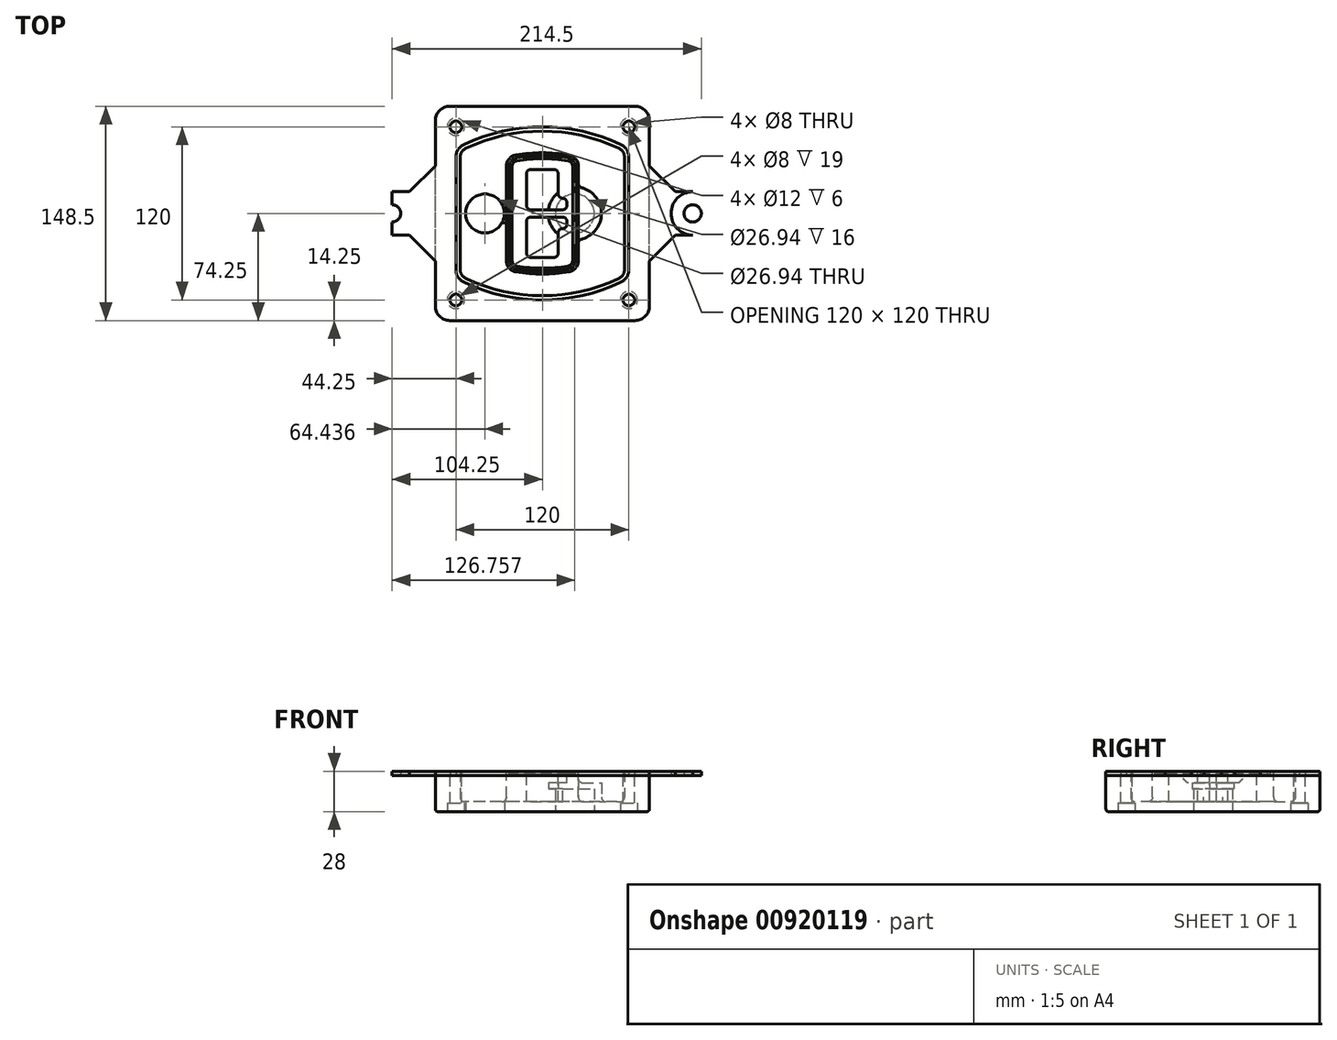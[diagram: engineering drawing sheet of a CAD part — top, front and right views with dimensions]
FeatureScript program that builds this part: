
annotation { "Feature Type Name" : "Feature", "Feature Type Description" : "" }
export const myFeature = defineFeature(function(context is Context, id is Id, definition is map)
    precondition{}
    {
        {
            var Q0;
            Q0=qCreatedBy(makeId("Top.planeOp"),FACE);
            var sketch = newSketch(context, id + "F0", { "sketchPlane" : qUnion([Q0])});
            skPoint(sketch, "E0.rect.middle", {"position": v(0, 0) * mm});
            skLineSegment(sketch, "E1.bottom", {"start": v(-64.25, -74.25) * mm, "end": v(64.25, -74.25) * mm});
            skLineSegment(sketch, "E1.top", {"start": v(-64.25, 74.25) * mm, "end": v(64.25, 74.25) * mm});
            skLineSegment(sketch, "E1.left", {"start": v(-74.25, -64.25) * mm, "end": v(-74.25, 64.25) * mm});
            skLineSegment(sketch, "E1.right", {"start": v(74.25, -64.25) * mm, "end": v(74.25, 64.25) * mm});
            skLineSegment(sketch, "E2", {"start": v(-74.25, 74.25) * mm, "end": v(74.25, -74.25) * mm, "construction": true});
            skLineSegment(sketch, "E3", {"start": v(74.25, 74.25) * mm, "end": v(-74.25, -74.25) * mm, "construction": true});
            skCircle(sketch, "E4", {"center": v(-60, 60) * mm, "radius": 4 * mm});
            skCircle(sketch, "E5", {"center": v(60, 60) * mm, "radius": 4 * mm});
            skCircle(sketch, "E6", {"center": v(60, -60) * mm, "radius": 4 * mm});
            skCircle(sketch, "E7", {"center": v(-60, -60) * mm, "radius": 4 * mm});
            skLineSegment(sketch, "E8", {"start": v(-60, 60) * mm, "end": v(60, 60) * mm, "construction": true});
            skLineSegment(sketch, "E9", {"start": v(60, 60) * mm, "end": v(60, -60) * mm, "construction": true});
            skLineSegment(sketch, "E10", {"start": v(60, -60) * mm, "end": v(-60, -60) * mm, "construction": true});
            skLineSegment(sketch, "E11", {"start": v(-60, -60) * mm, "end": v(-60, 60) * mm, "construction": true});
            skLineSegment(sketch, "E12", {"start": v(-60, 38.83) * mm, "end": v(-60, -38.83) * mm});
            skLineSegment(sketch, "E13", {"start": v(60, 38.83) * mm, "end": v(60, -38.83) * mm});
            skArc(sketch, "E14", {"start": v(54.26, 47.88) * mm, "mid": v(0, 60) * mm, "end": v(-54.26, 47.88) * mm});
            skArc(sketch, "E15", {"start": v(-54.26, -47.88) * mm, "mid": v(0, -60) * mm, "end": v(54.26, -47.88) * mm});
            skLineSegment(sketch, "E16", {"start": v(-60, 0) * mm, "end": v(60, 0) * mm, "construction": true});
            skPoint(sketch, "E17.visualSharp", {"position": v(-60, -45) * mm});
            skArc(sketch, "E17.filletArc", {"start": v(-60, -38.83) * mm, "mid": v(-58.44, -44.2) * mm, "end": v(-54.26, -47.88) * mm});
            skPoint(sketch, "E18.visualSharp", {"position": v(-60, 45) * mm});
            skArc(sketch, "E18.filletArc", {"start": v(-54.26, 47.88) * mm, "mid": v(-58.44, 44.2) * mm, "end": v(-60, 38.83) * mm});
            skPoint(sketch, "E19.visualSharp", {"position": v(60, 45) * mm});
            skArc(sketch, "E19.filletArc", {"start": v(60, 38.83) * mm, "mid": v(58.44, 44.2) * mm, "end": v(54.26, 47.88) * mm});
            skPoint(sketch, "E20.visualSharp", {"position": v(60, -45) * mm});
            skArc(sketch, "E20.filletArc", {"start": v(54.26, -47.88) * mm, "mid": v(58.44, -44.2) * mm, "end": v(60, -38.83) * mm});
            skPoint(sketch, "E21.visualSharp", {"position": v(-74.25, 74.25) * mm});
            skArc(sketch, "E21.filletArc", {"start": v(-64.25, 74.25) * mm, "mid": v(-71.32, 71.32) * mm, "end": v(-74.25, 64.25) * mm});
            skPoint(sketch, "E22.visualSharp", {"position": v(74.25, 74.25) * mm});
            skArc(sketch, "E22.filletArc", {"start": v(74.25, 64.25) * mm, "mid": v(71.32, 71.32) * mm, "end": v(64.25, 74.25) * mm});
            skPoint(sketch, "E23.visualSharp", {"position": v(74.25, -74.25) * mm});
            skArc(sketch, "E23.filletArc", {"start": v(64.25, -74.25) * mm, "mid": v(71.32, -71.32) * mm, "end": v(74.25, -64.25) * mm});
            skPoint(sketch, "E24.visualSharp", {"position": v(-74.25, -74.25) * mm});
            skArc(sketch, "E24.filletArc", {"start": v(-74.25, -64.25) * mm, "mid": v(-71.32, -71.32) * mm, "end": v(-64.25, -74.25) * mm});
            skArc(sketch, "E25.0", {"start": v(57, 38.83) * mm, "mid": v(55.9, 42.58) * mm, "end": v(52.98, 45.17) * mm});
            skLineSegment(sketch, "E25.1", {"start": v(57, 38.83) * mm, "end": v(57, -38.83) * mm});
            skArc(sketch, "E25.2", {"start": v(52.98, -45.17) * mm, "mid": v(55.9, -42.58) * mm, "end": v(57, -38.83) * mm});
            skArc(sketch, "E25.3", {"start": v(-52.98, -45.17) * mm, "mid": v(0, -57) * mm, "end": v(52.98, -45.17) * mm});
            skArc(sketch, "E25.4", {"start": v(-57, -38.83) * mm, "mid": v(-55.9, -42.58) * mm, "end": v(-52.98, -45.17) * mm});
            skArc(sketch, "E25.5", {"start": v(52.98, 45.17) * mm, "mid": v(0, 57) * mm, "end": v(-52.98, 45.17) * mm});
            skLineSegment(sketch, "E25.6", {"start": v(-57, 38.83) * mm, "end": v(-57, -38.83) * mm});
            skArc(sketch, "E25.7", {"start": v(-52.98, 45.17) * mm, "mid": v(-55.9, 42.58) * mm, "end": v(-57, 38.83) * mm});
            skArc(sketch, "E26.0", {"start": v(-55.96, 51.5) * mm, "mid": v(-61.82, 46.33) * mm, "end": v(-64, 38.83) * mm});
            skArc(sketch, "E26.1", {"start": v(55.96, 51.5) * mm, "mid": v(0, 64) * mm, "end": v(-55.96, 51.5) * mm});
            skArc(sketch, "E26.2", {"start": v(64, 38.83) * mm, "mid": v(61.82, 46.33) * mm, "end": v(55.96, 51.5) * mm});
            skLineSegment(sketch, "E26.3", {"start": v(64, 38.83) * mm, "end": v(64, -38.83) * mm});
            skArc(sketch, "E26.4", {"start": v(55.96, -51.5) * mm, "mid": v(61.82, -46.33) * mm, "end": v(64, -38.83) * mm});
            skLineSegment(sketch, "E26.5", {"start": v(-64, 38.83) * mm, "end": v(-64, -38.83) * mm});
            skArc(sketch, "E26.6", {"start": v(-55.96, -51.5) * mm, "mid": v(0, -64) * mm, "end": v(55.96, -51.5) * mm});
            skArc(sketch, "E26.7", {"start": v(-64, -38.83) * mm, "mid": v(-61.82, -46.33) * mm, "end": v(-55.96, -51.5) * mm});
            skSolve(sketch);
        }
        {
            var Q0;
            Q0=makeQuery(id+"F0.imprint","IMPRINT",FACE,{"disambiguationData":[TD([[makeQuery(id+"F0.imprint","IMPRINT",EDGE,{"derivedFrom":sQuery(id+"F0.wireOp",EDGE,"E1.bottom")}),1.0]])]});
            var Q1;
            Q1=makeQuery(id+"F0.imprint","IMPRINT",FACE,{"disambiguationData":[TD([[makeQuery(id+"F0.imprint","IMPRINT",EDGE,{"derivedFrom":sQuery(id+"F0.wireOp",EDGE,"E12")}),1.0]])]});
            var Q2;
            Q2=makeQuery(id+"F0.imprint","IMPRINT",FACE,{"disambiguationData":[TD([[makeQuery(id+"F0.imprint","IMPRINT",EDGE,{"derivedFrom":sQuery(id+"F0.wireOp",EDGE,"E25.0")}),1.0]])]});
            var Q3;
            Q3=makeQuery(id+"F0.imprint","IMPRINT",FACE,{"disambiguationData":[TD([[makeQuery(id+"F0.imprint","IMPRINT",EDGE,{"derivedFrom":sQuery(id+"F0.wireOp",EDGE,"E12")}),-1.0]])]});
            extrude(context, id + "F1", {"entities" : qUnion([Q0, Q1, Q2, Q3]), "oppositeDirection" : true, "depth" : 25 * mm});
        }
        {
            var Q0;
            Q0=makeQuery(id+"F0.imprint","IMPRINT",FACE,{"disambiguationData":[TD([[makeQuery(id+"F0.imprint","IMPRINT",EDGE,{"derivedFrom":sQuery(id+"F0.wireOp",EDGE,"E12")}),1.0]])]});
            extrude(context, id + "F2", {"entities" : qUnion([Q0]), "operationType" : NewBodyOperationType.ADD, "depth" : 3 * mm});
        }
        {
            var Q0;
            Q0=makeQuery(id+"F0.imprint","IMPRINT",FACE,{"disambiguationData":[TD([[makeQuery(id+"F0.imprint","IMPRINT",EDGE,{"derivedFrom":sQuery(id+"F0.wireOp",EDGE,"E25.0")}),1.0]])]});
            extrude(context, id + "F3", {"entities" : qUnion([Q0]), "operationType" : NewBodyOperationType.REMOVE, "oppositeDirection" : true, "depth" : 18 * mm});
        }
        {
            var Q0;
            Q0=makeQuery(id+"F2.opExtrude","CAP_FACE",FACE,{"disambiguationData":[OSD([sQuery(id+"F0.wireOp",EDGE,"E12"),sQuery(id+"F0.wireOp",EDGE,"E13"),sQuery(id+"F0.wireOp",EDGE,"E14"),sQuery(id+"F0.wireOp",EDGE,"E15"),sQuery(id+"F0.wireOp",EDGE,"E17.filletArc"),sQuery(id+"F0.wireOp",EDGE,"E18.filletArc"),sQuery(id+"F0.wireOp",EDGE,"E19.filletArc"),sQuery(id+"F0.wireOp",EDGE,"E20.filletArc"),sQuery(id+"F0.wireOp",EDGE,"E25.0"),sQuery(id+"F0.wireOp",EDGE,"E25.1"),sQuery(id+"F0.wireOp",EDGE,"E25.2"),sQuery(id+"F0.wireOp",EDGE,"E25.3"),sQuery(id+"F0.wireOp",EDGE,"E25.4"),sQuery(id+"F0.wireOp",EDGE,"E25.5"),sQuery(id+"F0.wireOp",EDGE,"E25.6"),sQuery(id+"F0.wireOp",EDGE,"E25.7")])],"isStart":false});
            var sketch = newSketch(context, id + "F4", { "sketchPlane" : qUnion([Q0])});
            skArc(sketch, "E27.0", {"start": v(-18.34, -40.45) * mm, "mid": v(0, -42) * mm, "end": v(18.34, -40.45) * mm});
            skArc(sketch, "E28.0", {"start": v(18.34, 40.45) * mm, "mid": v(0, 42) * mm, "end": v(-18.34, 40.45) * mm});
            skLineSegment(sketch, "E29", {"start": v(-25, 32.57) * mm, "end": v(-25, -32.57) * mm});
            skLineSegment(sketch, "E30", {"start": v(25, 32.57) * mm, "end": v(25, -32.57) * mm});
            skLineSegment(sketch, "E31", {"start": v(-25, 39.1) * mm, "end": v(25, 39.1) * mm, "construction": true});
            skLineSegment(sketch, "E32", {"start": v(-25, -39.1) * mm, "end": v(25, -39.1) * mm, "construction": true});
            skPoint(sketch, "E33.visualSharp", {"position": v(-25, 39.1) * mm});
            skArc(sketch, "E33.filletArc", {"start": v(-18.34, 40.45) * mm, "mid": v(-23.11, 37.73) * mm, "end": v(-25, 32.57) * mm});
            skPoint(sketch, "E34.visualSharp", {"position": v(25, 39.1) * mm});
            skArc(sketch, "E34.filletArc", {"start": v(25, 32.57) * mm, "mid": v(23.11, 37.73) * mm, "end": v(18.34, 40.45) * mm});
            skPoint(sketch, "E35.visualSharp", {"position": v(25, -39.1) * mm});
            skArc(sketch, "E35.filletArc", {"start": v(18.34, -40.45) * mm, "mid": v(23.11, -37.73) * mm, "end": v(25, -32.57) * mm});
            skPoint(sketch, "E36.visualSharp", {"position": v(-25, -39.1) * mm});
            skArc(sketch, "E36.filletArc", {"start": v(-25, -32.57) * mm, "mid": v(-23.11, -37.73) * mm, "end": v(-18.34, -40.45) * mm});
            skArc(sketch, "E37.0", {"start": v(52.98, 45.17) * mm, "mid": v(0, 57) * mm, "end": v(-52.98, 45.17) * mm});
            skArc(sketch, "E37.1", {"start": v(-52.98, 45.17) * mm, "mid": v(-55.9, 42.58) * mm, "end": v(-57, 38.83) * mm});
            skLineSegment(sketch, "E37.2", {"start": v(-57, 38.83) * mm, "end": v(-57, -38.83) * mm});
            skArc(sketch, "E37.3", {"start": v(-57, -38.83) * mm, "mid": v(-55.9, -42.58) * mm, "end": v(-52.98, -45.17) * mm});
            skArc(sketch, "E37.4", {"start": v(-52.98, -45.17) * mm, "mid": v(0, -57) * mm, "end": v(52.98, -45.17) * mm});
            skArc(sketch, "E37.5", {"start": v(52.98, -45.17) * mm, "mid": v(55.9, -42.58) * mm, "end": v(57, -38.83) * mm});
            skLineSegment(sketch, "E37.6", {"start": v(57, 38.83) * mm, "end": v(57, -38.83) * mm});
            skArc(sketch, "E37.7", {"start": v(57, 38.83) * mm, "mid": v(55.9, 42.58) * mm, "end": v(52.98, 45.17) * mm});
            skLineSegment(sketch, "E38.0", {"start": v(23, 32.57) * mm, "end": v(23, -32.57) * mm});
            skArc(sketch, "E38.1", {"start": v(18, -38.48) * mm, "mid": v(21.58, -36.44) * mm, "end": v(23, -32.57) * mm});
            skArc(sketch, "E38.2", {"start": v(-18, -38.48) * mm, "mid": v(0, -40) * mm, "end": v(18, -38.48) * mm});
            skArc(sketch, "E38.3", {"start": v(-23, -32.57) * mm, "mid": v(-21.58, -36.44) * mm, "end": v(-18, -38.48) * mm});
            skLineSegment(sketch, "E38.4", {"start": v(-23, 32.57) * mm, "end": v(-23, -32.57) * mm});
            skArc(sketch, "E38.5", {"start": v(23, 32.57) * mm, "mid": v(21.58, 36.44) * mm, "end": v(18, 38.48) * mm});
            skArc(sketch, "E38.6", {"start": v(-18, 38.48) * mm, "mid": v(-21.58, 36.44) * mm, "end": v(-23, 32.57) * mm});
            skArc(sketch, "E38.7", {"start": v(18, 38.48) * mm, "mid": v(0, 40) * mm, "end": v(-18, 38.48) * mm});
            skArc(sketch, "E39.0", {"start": v(21, 32.57) * mm, "mid": v(20.06, 35.15) * mm, "end": v(17.67, 36.5) * mm});
            skLineSegment(sketch, "E39.1", {"start": v(21, 32.57) * mm, "end": v(21, -32.57) * mm});
            skArc(sketch, "E39.2", {"start": v(17.67, -36.5) * mm, "mid": v(20.06, -35.15) * mm, "end": v(21, -32.57) * mm});
            skArc(sketch, "E39.3", {"start": v(-17.67, -36.5) * mm, "mid": v(0, -38) * mm, "end": v(17.67, -36.5) * mm});
            skArc(sketch, "E39.4", {"start": v(-21, -32.57) * mm, "mid": v(-20.06, -35.15) * mm, "end": v(-17.67, -36.5) * mm});
            skArc(sketch, "E39.5", {"start": v(17.67, 36.5) * mm, "mid": v(0, 38) * mm, "end": v(-17.67, 36.5) * mm});
            skLineSegment(sketch, "E39.6", {"start": v(-21, 32.57) * mm, "end": v(-21, -32.57) * mm});
            skArc(sketch, "E39.7", {"start": v(-17.67, 36.5) * mm, "mid": v(-20.06, 35.15) * mm, "end": v(-21, 32.57) * mm});
            skLineSegment(sketch, "E40", {"start": v(-25, 0) * mm, "end": v(25, 0) * mm, "construction": true});
            skLineSegment(sketch, "E41", {"start": v(-11, 5.5) * mm, "end": v(-11, 27.5) * mm});
            skLineSegment(sketch, "E42", {"start": v(-8, 30.5) * mm, "end": v(8, 30.5) * mm});
            skLineSegment(sketch, "E43", {"start": v(11, 27.5) * mm, "end": v(11, 13.5) * mm});
            skLineSegment(sketch, "E44", {"start": v(14, 10.5) * mm, "end": v(14, 10.5) * mm});
            skLineSegment(sketch, "E45", {"start": v(17, 7.5) * mm, "end": v(17, 5.5) * mm});
            skLineSegment(sketch, "E46", {"start": v(14, 2.5) * mm, "end": v(-8, 2.5) * mm});
            skPoint(sketch, "E47.visualSharp", {"position": v(-11, 30.5) * mm});
            skArc(sketch, "E47.filletArc", {"start": v(-8, 30.5) * mm, "mid": v(-10.12, 29.62) * mm, "end": v(-11, 27.5) * mm});
            skPoint(sketch, "E48.visualSharp", {"position": v(11, 30.5) * mm});
            skArc(sketch, "E48.filletArc", {"start": v(11, 27.5) * mm, "mid": v(10.12, 29.62) * mm, "end": v(8, 30.5) * mm});
            skPoint(sketch, "E49.visualSharp", {"position": v(11, 10.5) * mm});
            skArc(sketch, "E49.filletArc", {"start": v(11, 13.5) * mm, "mid": v(11.88, 11.38) * mm, "end": v(14, 10.5) * mm});
            skPoint(sketch, "E50.visualSharp", {"position": v(17, 10.5) * mm});
            skArc(sketch, "E50.filletArc", {"start": v(17, 7.5) * mm, "mid": v(16.12, 9.62) * mm, "end": v(14, 10.5) * mm});
            skPoint(sketch, "E51.visualSharp", {"position": v(17, 2.5) * mm});
            skArc(sketch, "E51.filletArc", {"start": v(14, 2.5) * mm, "mid": v(16.12, 3.38) * mm, "end": v(17, 5.5) * mm});
            skPoint(sketch, "E52.visualSharp", {"position": v(-11, 2.5) * mm});
            skArc(sketch, "E52.filletArc", {"start": v(-11, 5.5) * mm, "mid": v(-10.12, 3.38) * mm, "end": v(-8, 2.5) * mm});
            skLineSegment(sketch, "E53.0.MirrorCS", {"start": v(14, -2.5) * mm, "end": v(-8, -2.5) * mm});
            skArc(sketch, "E54.0.MirrorCS", {"start": v(-11, -5.5) * mm, "mid": v(-10.12, -3.38) * mm, "end": v(-8, -2.5) * mm});
            skLineSegment(sketch, "E55.0.MirrorCS", {"start": v(-11, -5.5) * mm, "end": v(-11, -27.5) * mm});
            skArc(sketch, "E56.0.MirrorCS", {"start": v(-8, -30.5) * mm, "mid": v(-10.12, -29.62) * mm, "end": v(-11, -27.5) * mm});
            skLineSegment(sketch, "E57.0.MirrorCS", {"start": v(-8, -30.5) * mm, "end": v(8, -30.5) * mm});
            skArc(sketch, "E58.0.MirrorCS", {"start": v(11, -27.5) * mm, "mid": v(10.12, -29.62) * mm, "end": v(8, -30.5) * mm});
            skLineSegment(sketch, "E59.0.MirrorCS", {"start": v(11, -27.5) * mm, "end": v(11, -13.5) * mm});
            skArc(sketch, "E60.0.MirrorCS", {"start": v(11, -13.5) * mm, "mid": v(11.88, -11.38) * mm, "end": v(14, -10.5) * mm});
            skArc(sketch, "E61.0.MirrorCS", {"start": v(17, -7.5) * mm, "mid": v(16.12, -9.62) * mm, "end": v(14, -10.5) * mm});
            skLineSegment(sketch, "E62.0.MirrorCS", {"start": v(17, -7.5) * mm, "end": v(17, -5.5) * mm});
            skArc(sketch, "E63.0.MirrorCS", {"start": v(14, -2.5) * mm, "mid": v(16.12, -3.38) * mm, "end": v(17, -5.5) * mm});
            skSolve(sketch);
        }
        {
            var Q0;
            Q0=makeQuery(id+"F4.imprint","IMPRINT",FACE,{"disambiguationData":[TD([[makeQuery(id+"F4.imprint","IMPRINT",EDGE,{"derivedFrom":sQuery(id+"F4.wireOp",EDGE,"E27.0")}),1.0]])]});
            var Q1;
            Q1=makeQuery(id+"F4.imprint","IMPRINT",FACE,{"disambiguationData":[TD([[makeQuery(id+"F4.imprint","IMPRINT",EDGE,{"derivedFrom":sQuery(id+"F4.wireOp",EDGE,"E38.0")}),-1.0]])]});
            var Q2;
            Q2=makeQuery(id+"F4.imprint","IMPRINT",FACE,{"disambiguationData":[TD([[makeQuery(id+"F4.imprint","IMPRINT",EDGE,{"derivedFrom":sQuery(id+"F4.wireOp",EDGE,"E39.0")}),1.0]])]});
            extrude(context, id + "F5", {"entities" : qUnion([Q0, Q1, Q2]), "operationType" : NewBodyOperationType.ADD, "endBound" : BoundingType.UP_TO_NEXT, "oppositeDirection" : true, "depth" : 25 * mm});
        }
        {
            var Q0;
            Q0=makeQuery(id+"F4.imprint","IMPRINT",FACE,{"disambiguationData":[TD([[makeQuery(id+"F4.imprint","IMPRINT",EDGE,{"derivedFrom":sQuery(id+"F4.wireOp",EDGE,"E38.0")}),-1.0]])]});
            extrude(context, id + "F6", {"entities" : qUnion([Q0]), "operationType" : NewBodyOperationType.REMOVE, "oppositeDirection" : true, "depth" : 2 * mm});
        }
        {
            var Q0;
            Q0=makeQuery(id+"F1.opExtrude","CAP_FACE",FACE,{"disambiguationData":[OSD([sQuery(id+"F0.wireOp",EDGE,"E1.bottom"),sQuery(id+"F0.wireOp",EDGE,"E1.top"),sQuery(id+"F0.wireOp",EDGE,"E1.left"),sQuery(id+"F0.wireOp",EDGE,"E1.right"),sQuery(id+"F0.wireOp",EDGE,"E4"),sQuery(id+"F0.wireOp",EDGE,"E5"),sQuery(id+"F0.wireOp",EDGE,"E6"),sQuery(id+"F0.wireOp",EDGE,"E7"),sQuery(id+"F0.wireOp",EDGE,"E21.filletArc"),sQuery(id+"F0.wireOp",EDGE,"E22.filletArc"),sQuery(id+"F0.wireOp",EDGE,"E23.filletArc"),sQuery(id+"F0.wireOp",EDGE,"E24.filletArc")])],"isStart":false});
            var sketch = newSketch(context, id + "F7", { "sketchPlane" : qUnion([Q0])});
            skCircle(sketch, "E64", {"center": v(22.5, 0) * mm, "radius": 13.47 * mm});
            skCircle(sketch, "E65", {"center": v(-39.81, 0) * mm, "radius": 13.47 * mm});
            skLineSegment(sketch, "E66", {"start": v(74.25, 0) * mm, "end": v(-74.25, 0) * mm});
            skCircle(sketch, "E67", {"center": v(22.5, 0) * mm, "radius": 18.47 * mm});
            skCircle(sketch, "E68", {"center": v(60, -60) * mm, "radius": 6 * mm});
            skCircle(sketch, "E69", {"center": v(-60, -60) * mm, "radius": 6 * mm});
            skCircle(sketch, "E70", {"center": v(-60, 60) * mm, "radius": 6 * mm});
            skCircle(sketch, "E71", {"center": v(60, 60) * mm, "radius": 6 * mm});
            skSolve(sketch);
        }
        {
            var Q0;
            {var subQ1=sQuery(id+"F7.wireOp",EDGE,"E66");var subQ4=sQuery(id+"F7.wireOp",EDGE,"E64");var subQ6=makeQuery(id+"F7.imprint","INTERSECT",VERTEX,{"disambiguationData":[OD(0.0)],"derivedFrom":[subQ4,subQ1]});Q0=makeQuery(id+"F7.imprint","IMPRINT",FACE,{"disambiguationData":[TD([[makeQuery(id+"F7.imprint","IMPRINT",EDGE,{"disambiguationData":[TD([[subQ6,-1.0]])],"derivedFrom":subQ4}),-1.0]])]});}
            var Q1;
            {var subQ0=sQuery(id+"F7.wireOp",EDGE,"E66");var subQ1=sQuery(id+"F7.wireOp",EDGE,"E64");var subQ3=makeQuery(id+"F7.imprint","INTERSECT",VERTEX,{"disambiguationData":[OD(0.0)],"derivedFrom":[subQ1,subQ0]});Q1=makeQuery(id+"F7.imprint","IMPRINT",FACE,{"disambiguationData":[TD([[makeQuery(id+"F7.imprint","IMPRINT",EDGE,{"disambiguationData":[TD([[subQ3,-1.0]])],"derivedFrom":subQ1}),1.0]])]});}
            var Q2;
            {var subQ0=sQuery(id+"F7.wireOp",EDGE,"E66");var subQ1=sQuery(id+"F7.wireOp",EDGE,"E64");var subQ3=makeQuery(id+"F7.imprint","INTERSECT",VERTEX,{"disambiguationData":[OD(0.0)],"derivedFrom":[subQ1,subQ0]});Q2=makeQuery(id+"F7.imprint","IMPRINT",FACE,{"disambiguationData":[TD([[makeQuery(id+"F7.imprint","IMPRINT",EDGE,{"disambiguationData":[TD([[subQ3,1.0]])],"derivedFrom":subQ1}),1.0]])]});}
            var Q3;
            {var subQ1=sQuery(id+"F7.wireOp",EDGE,"E66");var subQ4=sQuery(id+"F7.wireOp",EDGE,"E64");var subQ6=makeQuery(id+"F7.imprint","INTERSECT",VERTEX,{"disambiguationData":[OD(0.0)],"derivedFrom":[subQ4,subQ1]});Q3=makeQuery(id+"F7.imprint","IMPRINT",FACE,{"disambiguationData":[TD([[makeQuery(id+"F7.imprint","IMPRINT",EDGE,{"disambiguationData":[TD([[subQ6,1.0]])],"derivedFrom":subQ4}),-1.0]])]});}
            extrude(context, id + "F8", {"entities" : qUnion([Q0, Q1, Q2, Q3]), "operationType" : NewBodyOperationType.ADD, "oppositeDirection" : true, "depth" : 20 * mm});
        }
        {
            var Q0;
            {var subQ0=sQuery(id+"F7.wireOp",EDGE,"E66");var subQ1=sQuery(id+"F7.wireOp",EDGE,"E64");var subQ3=makeQuery(id+"F7.imprint","INTERSECT",VERTEX,{"disambiguationData":[OD(0.0)],"derivedFrom":[subQ1,subQ0]});Q0=makeQuery(id+"F7.imprint","IMPRINT",FACE,{"disambiguationData":[TD([[makeQuery(id+"F7.imprint","IMPRINT",EDGE,{"disambiguationData":[TD([[subQ3,-1.0]])],"derivedFrom":subQ1}),1.0]])]});}
            var Q1;
            {var subQ0=sQuery(id+"F7.wireOp",EDGE,"E66");var subQ1=sQuery(id+"F7.wireOp",EDGE,"E64");var subQ3=makeQuery(id+"F7.imprint","INTERSECT",VERTEX,{"disambiguationData":[OD(0.0)],"derivedFrom":[subQ1,subQ0]});Q1=makeQuery(id+"F7.imprint","IMPRINT",FACE,{"disambiguationData":[TD([[makeQuery(id+"F7.imprint","IMPRINT",EDGE,{"disambiguationData":[TD([[subQ3,1.0]])],"derivedFrom":subQ1}),1.0]])]});}
            extrude(context, id + "F9", {"entities" : qUnion([Q0, Q1]), "operationType" : NewBodyOperationType.REMOVE, "oppositeDirection" : true, "depth" : 16 * mm});
        }
        {
            var Q0;
            {var subQ0=sQuery(id+"F7.wireOp",EDGE,"E66");var subQ1=sQuery(id+"F7.wireOp",EDGE,"E65");var subQ3=makeQuery(id+"F7.imprint","INTERSECT",VERTEX,{"disambiguationData":[OD(0.0)],"derivedFrom":[subQ1,subQ0]});Q0=makeQuery(id+"F7.imprint","IMPRINT",FACE,{"disambiguationData":[TD([[makeQuery(id+"F7.imprint","IMPRINT",EDGE,{"disambiguationData":[TD([[subQ3,-1.0]])],"derivedFrom":subQ1}),1.0]])]});}
            var Q1;
            {var subQ0=sQuery(id+"F7.wireOp",EDGE,"E66");var subQ1=sQuery(id+"F7.wireOp",EDGE,"E65");var subQ3=makeQuery(id+"F7.imprint","INTERSECT",VERTEX,{"disambiguationData":[OD(0.0)],"derivedFrom":[subQ1,subQ0]});Q1=makeQuery(id+"F7.imprint","IMPRINT",FACE,{"disambiguationData":[TD([[makeQuery(id+"F7.imprint","IMPRINT",EDGE,{"disambiguationData":[TD([[subQ3,1.0]])],"derivedFrom":subQ1}),1.0]])]});}
            extrude(context, id + "F10", {"entities" : qUnion([Q0, Q1]), "operationType" : NewBodyOperationType.REMOVE, "oppositeDirection" : true, "depth" : 25 * mm});
        }
        {
            var Q0;
            Q0=makeQuery(id+"F7.imprint","IMPRINT",FACE,{"disambiguationData":[TD([[makeQuery(id+"F7.imprint","IMPRINT",EDGE,{"derivedFrom":sQuery(id+"F7.wireOp",EDGE,"E68")}),1.0]])]});
            var Q1;
            Q1=makeQuery(id+"F7.imprint","IMPRINT",FACE,{"disambiguationData":[TD([[makeQuery(id+"F7.imprint","IMPRINT",EDGE,{"derivedFrom":makeQuery(id+"F1.opExtrude","CAP_EDGE",EDGE,{"disambiguationData":[OSD([sQuery(id+"F0.wireOp",EDGE,"E5")])],"isStart":false})}),-1.0]])]});
            var Q2;
            Q2=makeQuery(id+"F7.imprint","IMPRINT",FACE,{"disambiguationData":[TD([[makeQuery(id+"F7.imprint","IMPRINT",EDGE,{"derivedFrom":sQuery(id+"F7.wireOp",EDGE,"E69")}),1.0]])]});
            var Q3;
            Q3=makeQuery(id+"F7.imprint","IMPRINT",FACE,{"disambiguationData":[TD([[makeQuery(id+"F7.imprint","IMPRINT",EDGE,{"derivedFrom":makeQuery(id+"F1.opExtrude","CAP_EDGE",EDGE,{"disambiguationData":[OSD([sQuery(id+"F0.wireOp",EDGE,"E4")])],"isStart":false})}),-1.0]])]});
            var Q4;
            Q4=makeQuery(id+"F7.imprint","IMPRINT",FACE,{"disambiguationData":[TD([[makeQuery(id+"F7.imprint","IMPRINT",EDGE,{"derivedFrom":sQuery(id+"F7.wireOp",EDGE,"E70")}),1.0]])]});
            var Q5;
            Q5=makeQuery(id+"F7.imprint","IMPRINT",FACE,{"disambiguationData":[TD([[makeQuery(id+"F7.imprint","IMPRINT",EDGE,{"derivedFrom":makeQuery(id+"F1.opExtrude","CAP_EDGE",EDGE,{"disambiguationData":[OSD([sQuery(id+"F0.wireOp",EDGE,"E7")])],"isStart":false})}),-1.0]])]});
            var Q6;
            Q6=makeQuery(id+"F7.imprint","IMPRINT",FACE,{"disambiguationData":[TD([[makeQuery(id+"F7.imprint","IMPRINT",EDGE,{"derivedFrom":sQuery(id+"F7.wireOp",EDGE,"E71")}),1.0]])]});
            var Q7;
            Q7=makeQuery(id+"F7.imprint","IMPRINT",FACE,{"disambiguationData":[TD([[makeQuery(id+"F7.imprint","IMPRINT",EDGE,{"derivedFrom":makeQuery(id+"F1.opExtrude","CAP_EDGE",EDGE,{"disambiguationData":[OSD([sQuery(id+"F0.wireOp",EDGE,"E6")])],"isStart":false})}),-1.0]])]});
            extrude(context, id + "F11", {"entities" : qUnion([Q0, Q1, Q2, Q3, Q4, Q5, Q6, Q7]), "operationType" : NewBodyOperationType.REMOVE, "oppositeDirection" : true, "depth" : 6 * mm});
        }
        {
            var Q0;
            Q0=makeQuery(id+"F9.boolean.opBoolean","COPY",FACE,{"derivedFrom":makeQuery(id+"F9.opExtrude","CAP_FACE",FACE,{"disambiguationData":[OSD([sQuery(id+"F7.wireOp",EDGE,"E64")])],"isStart":false})});
            var sketch = newSketch(context, id + "F12", { "sketchPlane" : qUnion([Q0])});
            skArc(sketch, "E72.0", {"start": v(11, 14.45) * mm, "mid": v(6.45, 9.13) * mm, "end": v(4.2, 2.5) * mm});
            skArc(sketch, "E72.1", {"start": v(4.2, -2.5) * mm, "mid": v(6.45, -9.13) * mm, "end": v(11, -14.45) * mm});
            skLineSegment(sketch, "E73", {"start": v(4.2, -2.5) * mm, "end": v(14, -2.5) * mm});
            skLineSegment(sketch, "E74.0", {"start": v(14, 2.5) * mm, "end": v(4.2, 2.5) * mm});
            skArc(sketch, "E74.1", {"start": v(14, 2.5) * mm, "mid": v(16.12, 3.38) * mm, "end": v(17, 5.5) * mm});
            skLineSegment(sketch, "E74.2", {"start": v(17, 7.5) * mm, "end": v(17, 5.5) * mm});
            skArc(sketch, "E74.3", {"start": v(17, 7.5) * mm, "mid": v(16.12, 9.62) * mm, "end": v(14, 10.5) * mm});
            skArc(sketch, "E74.4", {"start": v(11, 13.5) * mm, "mid": v(11.88, 11.38) * mm, "end": v(14, 10.5) * mm});
            skLineSegment(sketch, "E74.5", {"start": v(11, 14.45) * mm, "end": v(11, 13.5) * mm});
            skLineSegment(sketch, "E74.7", {"start": v(14, -2.5) * mm, "end": v(4.2, -2.5) * mm});
            skArc(sketch, "E74.8", {"start": v(14, -2.5) * mm, "mid": v(16.12, -3.38) * mm, "end": v(17, -5.5) * mm});
            skLineSegment(sketch, "E74.9", {"start": v(17, -7.5) * mm, "end": v(17, -5.5) * mm});
            skArc(sketch, "E74.10", {"start": v(17, -7.5) * mm, "mid": v(16.12, -9.62) * mm, "end": v(14, -10.5) * mm});
            skArc(sketch, "E74.11", {"start": v(11, -13.5) * mm, "mid": v(11.88, -11.38) * mm, "end": v(14, -10.5) * mm});
            skLineSegment(sketch, "E74.12", {"start": v(11, -14.45) * mm, "end": v(11, -13.5) * mm});
            skPoint(sketch, "E75.orphan", {"position": v(11, -27.5) * mm});
            skPoint(sketch, "E76.orphan", {"position": v(-8, -2.5) * mm});
            skPoint(sketch, "E77.orphan", {"position": v(-8, 2.5) * mm});
            skPoint(sketch, "E78.orphan", {"position": v(11, 27.5) * mm});
            skSolve(sketch);
        }
        {
            var Q0;
            {var subQ7=sQuery(id+"F12.wireOp",EDGE,"E72.0");var subQ14=sQuery(id+"F12.wireOp",EDGE,"E72.1");var subQ16=sQuery(id+"F12.wireOp",EDGE,"E74.1");var subQ18=sQuery(id+"F12.wireOp",EDGE,"E74.8");Q0=qUnion([makeQuery(id+"F12.imprint","IMPRINT",FACE,{"disambiguationData":[TD([[makeQuery(id+"F12.imprint","IMPRINT",EDGE,{"derivedFrom":subQ7}),1.0]])]}),makeQuery(id+"F12.imprint","IMPRINT",FACE,{"disambiguationData":[TD([[makeQuery(id+"F12.imprint","IMPRINT",EDGE,{"derivedFrom":subQ14}),1.0]])]}),makeQuery(id+"F12.imprint","IMPRINT",FACE,{"disambiguationData":[TD([[makeQuery(id+"F12.imprint","IMPRINT",EDGE,{"derivedFrom":subQ16}),1.0]])]}),makeQuery(id+"F12.imprint","IMPRINT",FACE,{"disambiguationData":[TD([[makeQuery(id+"F12.imprint","IMPRINT",EDGE,{"derivedFrom":subQ18}),-1.0]])]})]);}
            var Q1;
            Q1=makeQuery(id+"F5.boolean.opBoolean","SPLIT",FACE,{"disambiguationData":[TD([makeQuery(id+"F5.opExtrude","SWEPT_FACE",FACE,{"disambiguationData":[OSD([sQuery(id+"F4.wireOp",EDGE,"E41")])]})])],"derivedFrom":makeQuery(id+"F3.boolean.opBoolean","COPY",FACE,{"derivedFrom":makeQuery(id+"F3.opExtrude","CAP_FACE",FACE,{"disambiguationData":[OSD([sQuery(id+"F0.wireOp",EDGE,"E25.0"),sQuery(id+"F0.wireOp",EDGE,"E25.1"),sQuery(id+"F0.wireOp",EDGE,"E25.2"),sQuery(id+"F0.wireOp",EDGE,"E25.3"),sQuery(id+"F0.wireOp",EDGE,"E25.4"),sQuery(id+"F0.wireOp",EDGE,"E25.5"),sQuery(id+"F0.wireOp",EDGE,"E25.6"),sQuery(id+"F0.wireOp",EDGE,"E25.7")])],"isStart":false})})});
            extrude(context, id + "F13", {"entities" : qUnion([Q0]), "operationType" : NewBodyOperationType.REMOVE, "endBound" : BoundingType.UP_TO_SURFACE, "endBoundEntityFace" : qUnion([Q1]), "depth" : 25 * mm});
        }
        {
            var Q0;
            Q0=makeQuery(id+"F3.boolean.opBoolean","COPY",EDGE,{"derivedFrom":makeQuery(id+"F3.opExtrude","CAP_EDGE",EDGE,{"disambiguationData":[OSD([sQuery(id+"F0.wireOp",EDGE,"E25.6")])],"isStart":false})});
            var Q1;
            Q1=makeQuery(id+"F8.boolean.opBoolean","INTERSECT",EDGE,{"derivedFrom":[makeQuery(id+"F5.opExtrude","SWEPT_FACE",FACE,{"disambiguationData":[OSD([sQuery(id+"F4.wireOp",EDGE,"E30")])]}),makeQuery(id+"F8.opExtrude","CAP_FACE",FACE,{"disambiguationData":[OSD([sQuery(id+"F7.wireOp",EDGE,"E67")])],"isStart":false})]});
            var Q2;
            Q2=makeQuery(id+"F8.boolean.opBoolean","INTERSECT",EDGE,{"disambiguationData":[OD(1.0)],"derivedFrom":[makeQuery(id+"F5.opExtrude","SWEPT_FACE",FACE,{"disambiguationData":[OSD([sQuery(id+"F4.wireOp",EDGE,"E30")])]}),makeQuery(id+"F8.opExtrude","SWEPT_FACE",FACE,{"disambiguationData":[OSD([sQuery(id+"F7.wireOp",EDGE,"E67")])]})]});
            var Q3;
            {var subQ0=sQuery(id+"F4.wireOp",EDGE,"E30");Q3=makeQuery(id+"F8.boolean.opBoolean","SPLIT",EDGE,{"disambiguationData":[TD([makeQuery(id+"F5.opExtrude","SWEPT_FACE",FACE,{"disambiguationData":[OSD([sQuery(id+"F4.wireOp",EDGE,"E35.filletArc")])]})])],"derivedFrom":makeQuery(id+"F5.opExtrude","CAP_EDGE",EDGE,{"disambiguationData":[OSD([subQ0])],"isStart":false})});}
            var Q4;
            {var subQ0=sQuery(id+"F0.wireOp",EDGE,"E25.7");var subQ1=sQuery(id+"F0.wireOp",EDGE,"E25.1");var subQ2=sQuery(id+"F0.wireOp",EDGE,"E25.6");var subQ3=sQuery(id+"F0.wireOp",EDGE,"E25.5");var subQ4=sQuery(id+"F0.wireOp",EDGE,"E25.4");var subQ5=sQuery(id+"F0.wireOp",EDGE,"E25.0");var subQ6=sQuery(id+"F0.wireOp",EDGE,"E25.2");var subQ7=sQuery(id+"F0.wireOp",EDGE,"E25.3");Q4=makeQuery(id+"F8.boolean.opBoolean","INTERSECT",EDGE,{"derivedFrom":[makeQuery(id+"F5.boolean.opBoolean","SPLIT",FACE,{"disambiguationData":[TD([makeQuery(id+"F2.opExtrude","SWEPT_FACE",FACE,{"disambiguationData":[OSD([subQ5])]})])],"derivedFrom":makeQuery(id+"F3.boolean.opBoolean","COPY",FACE,{"derivedFrom":makeQuery(id+"F3.opExtrude","CAP_FACE",FACE,{"disambiguationData":[OSD([subQ5,subQ1,subQ6,subQ7,subQ4,subQ3,subQ2,subQ0])],"isStart":false})})}),makeQuery(id+"F8.opExtrude","SWEPT_FACE",FACE,{"disambiguationData":[OSD([sQuery(id+"F7.wireOp",EDGE,"E67")])]})]});}
            var Q5;
            Q5=makeQuery(id+"F8.boolean.opBoolean","INTERSECT",EDGE,{"disambiguationData":[OD(0.0)],"derivedFrom":[makeQuery(id+"F5.opExtrude","SWEPT_FACE",FACE,{"disambiguationData":[OSD([sQuery(id+"F4.wireOp",EDGE,"E30")])]}),makeQuery(id+"F8.opExtrude","SWEPT_FACE",FACE,{"disambiguationData":[OSD([sQuery(id+"F7.wireOp",EDGE,"E67")])]})]});
            fillet(context, id + "F14", {"entities" : qUnion([Q0, Q1, Q2, Q3, Q4, Q5]), "radius" : 3 * mm, "tangentPropagation" : true, "allowEdgeOverflow" : false});
        }
        {
            var Q0;
            Q0=makeQuery(id+"F1.opExtrude","CAP_EDGE",EDGE,{"disambiguationData":[OSD([sQuery(id+"F0.wireOp",EDGE,"E1.bottom")])],"isStart":false});
            fillet(context, id + "F15", {"entities" : qUnion([Q0]), "radius" : 2 * mm, "tangentPropagation" : true, "allowEdgeOverflow" : false});
        }
        {
            var Q0;
            {var subQ0=sQuery(id+"F0.wireOp",EDGE,"E21.filletArc");var subQ1=sQuery(id+"F0.wireOp",EDGE,"E7");var subQ2=sQuery(id+"F0.wireOp",EDGE,"E6");var subQ3=sQuery(id+"F0.wireOp",EDGE,"E5");var subQ4=sQuery(id+"F0.wireOp",EDGE,"E4");var subQ5=sQuery(id+"F0.wireOp",EDGE,"E22.filletArc");var subQ6=sQuery(id+"F0.wireOp",EDGE,"E1.bottom");var subQ7=sQuery(id+"F0.wireOp",EDGE,"E1.right");var subQ8=sQuery(id+"F0.wireOp",EDGE,"E1.top");var subQ9=sQuery(id+"F0.wireOp",EDGE,"E1.left");var subQ10=sQuery(id+"F0.wireOp",EDGE,"E23.filletArc");var subQ11=sQuery(id+"F0.wireOp",EDGE,"E24.filletArc");Q0=makeQuery(id+"F2.boolean.opBoolean","SPLIT",FACE,{"disambiguationData":[TD([makeQuery(id+"F1.opExtrude","SWEPT_FACE",FACE,{"disambiguationData":[OSD([subQ6])]})])],"derivedFrom":makeQuery(id+"F1.opExtrude","CAP_FACE",FACE,{"disambiguationData":[OSD([subQ6,subQ8,subQ9,subQ7,subQ4,subQ3,subQ2,subQ1,subQ0,subQ5,subQ10,subQ11])],"isStart":true})});}
            var sketch = newSketch(context, id + "F16", { "sketchPlane" : qUnion([Q0])});
            skLineSegment(sketch, "E79.0", {"start": v(74.25, -64.25) * mm, "end": v(74.25, 64.25) * mm});
            skArc(sketch, "E79.1", {"start": v(64.25, -74.25) * mm, "mid": v(71.32, -71.32) * mm, "end": v(74.25, -64.25) * mm});
            skLineSegment(sketch, "E79.2", {"start": v(-64.25, -74.25) * mm, "end": v(64.25, -74.25) * mm});
            skArc(sketch, "E79.3", {"start": v(-74.25, -64.25) * mm, "mid": v(-71.32, -71.32) * mm, "end": v(-64.25, -74.25) * mm});
            skLineSegment(sketch, "E79.4", {"start": v(-74.25, -64.25) * mm, "end": v(-74.25, 64.25) * mm});
            skArc(sketch, "E79.5", {"start": v(-64.25, 74.25) * mm, "mid": v(-71.32, 71.32) * mm, "end": v(-74.25, 64.25) * mm});
            skLineSegment(sketch, "E79.6", {"start": v(-64.25, 74.25) * mm, "end": v(64.25, 74.25) * mm});
            skArc(sketch, "E79.7", {"start": v(74.25, 64.25) * mm, "mid": v(71.32, 71.32) * mm, "end": v(64.25, 74.25) * mm});
            skLineSegment(sketch, "E79.8", {"start": v(60, 38.83) * mm, "end": v(60, -38.83) * mm});
            skArc(sketch, "E79.9", {"start": v(54.26, 47.88) * mm, "mid": v(0, 60) * mm, "end": v(-54.26, 47.88) * mm});
            skArc(sketch, "E79.10", {"start": v(60, 38.83) * mm, "mid": v(58.44, 44.2) * mm, "end": v(54.26, 47.88) * mm});
            skLineSegment(sketch, "E79.11", {"start": v(-60, 38.83) * mm, "end": v(-60, -38.83) * mm});
            skArc(sketch, "E79.12", {"start": v(-54.26, 47.88) * mm, "mid": v(-58.44, 44.2) * mm, "end": v(-60, 38.83) * mm});
            skArc(sketch, "E79.13", {"start": v(-60, -38.83) * mm, "mid": v(-58.44, -44.2) * mm, "end": v(-54.26, -47.88) * mm});
            skArc(sketch, "E79.14", {"start": v(-54.26, -47.88) * mm, "mid": v(0, -60) * mm, "end": v(54.26, -47.88) * mm});
            skArc(sketch, "E79.15", {"start": v(54.26, -47.88) * mm, "mid": v(58.44, -44.2) * mm, "end": v(60, -38.83) * mm});
            skCircle(sketch, "E79.16", {"center": v(60, -60) * mm, "radius": 4 * mm});
            skCircle(sketch, "E79.17", {"center": v(60, 60) * mm, "radius": 4 * mm});
            skCircle(sketch, "E79.18", {"center": v(-60, 60) * mm, "radius": 4 * mm});
            skCircle(sketch, "E79.19", {"center": v(-60, -60) * mm, "radius": 4 * mm});
            skLineSegment(sketch, "E80", {"start": v(-137.52, 0) * mm, "end": v(105.83, 0) * mm, "construction": true});
            skPoint(sketch, "E80.endSnap0", {"position": v(74.25, 0) * mm});
            skLineSegment(sketch, "E81", {"start": v(-74.25, 33) * mm, "end": v(-92.25, 15) * mm});
            skLineSegment(sketch, "E82", {"start": v(-92.25, 15) * mm, "end": v(-104.25, 15) * mm});
            skLineSegment(sketch, "E83", {"start": v(-104.25, 15) * mm, "end": v(-104.25, -15) * mm});
            skLineSegment(sketch, "E84", {"start": v(-104.25, -15) * mm, "end": v(-92.25, -15) * mm});
            skLineSegment(sketch, "E85", {"start": v(-92.25, -15) * mm, "end": v(-74.25, -33) * mm});
            skLineSegment(sketch, "E86", {"start": v(-104.25, 0) * mm, "end": v(-74.25, 0) * mm});
            skCircle(sketch, "E87", {"center": v(-104.25, 0) * mm, "radius": 15 * mm});
            skCircle(sketch, "E88", {"center": v(-104.25, 0) * mm, "radius": 6 * mm});
            skLineSegment(sketch, "E89", {"start": v(0, 104.96) * mm, "end": v(0, -108.19) * mm, "construction": true});
            skPoint(sketch, "E89.startSnap0", {"position": v(0, 74.25) * mm});
            skPoint(sketch, "E89.endSnap0", {"position": v(0, -74.25) * mm});
            skCircle(sketch, "E90.MirrorC", {"center": v(104.25, 0) * mm, "radius": 6 * mm});
            skLineSegment(sketch, "E91.MirrorCS", {"start": v(92.25, -15) * mm, "end": v(74.25, -33) * mm});
            skLineSegment(sketch, "E92.MirrorCS", {"start": v(104.25, -15) * mm, "end": v(92.25, -15) * mm});
            skCircle(sketch, "E93.MirrorC", {"center": v(104.25, 0) * mm, "radius": 15 * mm});
            skLineSegment(sketch, "E94.MirrorCS", {"start": v(74.25, 33) * mm, "end": v(92.25, 15) * mm});
            skLineSegment(sketch, "E95.MirrorCS", {"start": v(92.25, 15) * mm, "end": v(104.25, 15) * mm});
            skSolve(sketch);
        }
        {
            var Q0;
            {var subQ5=sQuery(id+"F16.wireOp",EDGE,"E84");Q0=makeQuery(id+"F16.imprint","IMPRINT",FACE,{"disambiguationData":[TD([[makeQuery(id+"F16.imprint","IMPRINT",EDGE,{"derivedFrom":subQ5}),1.0]])]});}
            var Q1;
            {var subQ3=sQuery(id+"F16.wireOp",EDGE,"E88");var subQ5=sQuery(id+"F16.wireOp",EDGE,"E86");var subQ6=makeQuery(id+"F16.imprint","INTERSECT",VERTEX,{"derivedFrom":[subQ5,subQ3]});Q1=makeQuery(id+"F16.imprint","IMPRINT",FACE,{"disambiguationData":[TD([[makeQuery(id+"F16.imprint","IMPRINT",EDGE,{"disambiguationData":[TD([[subQ6,-1.0]])],"derivedFrom":subQ5}),-1.0]])]});}
            var Q2;
            {var subQ1=sQuery(id+"F16.wireOp",EDGE,"E83");var subQ3=sQuery(id+"F16.wireOp",EDGE,"E88");var subQ4=makeQuery(id+"F16.imprint","INTERSECT",VERTEX,{"disambiguationData":[OD(0.0)],"derivedFrom":[subQ1,subQ3]});Q2=makeQuery(id+"F16.imprint","IMPRINT",FACE,{"disambiguationData":[TD([[makeQuery(id+"F16.imprint","IMPRINT",EDGE,{"disambiguationData":[TD([[subQ4,-1.0]])],"derivedFrom":subQ3}),-1.0]])]});}
            var Q3;
            {var subQ3=sQuery(id+"F16.wireOp",EDGE,"E88");var subQ5=sQuery(id+"F16.wireOp",EDGE,"E86");var subQ6=makeQuery(id+"F16.imprint","INTERSECT",VERTEX,{"derivedFrom":[subQ5,subQ3]});Q3=makeQuery(id+"F16.imprint","IMPRINT",FACE,{"disambiguationData":[TD([[makeQuery(id+"F16.imprint","IMPRINT",EDGE,{"disambiguationData":[TD([[subQ6,-1.0]])],"derivedFrom":subQ5}),1.0]])]});}
            var Q4;
            {var subQ6=sQuery(id+"F16.wireOp",EDGE,"E81");Q4=makeQuery(id+"F16.imprint","IMPRINT",FACE,{"disambiguationData":[TD([[makeQuery(id+"F16.imprint","IMPRINT",EDGE,{"derivedFrom":subQ6}),1.0]])]});}
            var Q5;
            {var subQ1=sQuery(id+"F16.wireOp",EDGE,"E91.MirrorCS");Q5=makeQuery(id+"F16.imprint","IMPRINT",FACE,{"disambiguationData":[TD([[makeQuery(id+"F16.imprint","IMPRINT",EDGE,{"derivedFrom":subQ1}),-1.0]])]});}
            var Q6;
            Q6=makeQuery(id+"F16.imprint","IMPRINT",FACE,{"disambiguationData":[TD([[makeQuery(id+"F16.imprint","IMPRINT",EDGE,{"derivedFrom":sQuery(id+"F16.wireOp",EDGE,"E90.MirrorC")}),1.0]])]});
            var Q7;
            {var subQ2=sQuery(id+"F16.wireOp",EDGE,"E79.1");Q7=makeQuery(id+"F16.imprint","IMPRINT",FACE,{"disambiguationData":[TD([[makeQuery(id+"F16.imprint","IMPRINT",EDGE,{"derivedFrom":subQ2}),1.0]])]});}
            var Q8;
            Q8=makeQuery(id+"F2.opExtrude","CAP_FACE",FACE,{"disambiguationData":[OSD([sQuery(id+"F0.wireOp",EDGE,"E12"),sQuery(id+"F0.wireOp",EDGE,"E13"),sQuery(id+"F0.wireOp",EDGE,"E14"),sQuery(id+"F0.wireOp",EDGE,"E15"),sQuery(id+"F0.wireOp",EDGE,"E17.filletArc"),sQuery(id+"F0.wireOp",EDGE,"E18.filletArc"),sQuery(id+"F0.wireOp",EDGE,"E19.filletArc"),sQuery(id+"F0.wireOp",EDGE,"E20.filletArc"),sQuery(id+"F0.wireOp",EDGE,"E25.0"),sQuery(id+"F0.wireOp",EDGE,"E25.1"),sQuery(id+"F0.wireOp",EDGE,"E25.2"),sQuery(id+"F0.wireOp",EDGE,"E25.3"),sQuery(id+"F0.wireOp",EDGE,"E25.4"),sQuery(id+"F0.wireOp",EDGE,"E25.5"),sQuery(id+"F0.wireOp",EDGE,"E25.6"),sQuery(id+"F0.wireOp",EDGE,"E25.7")])],"isStart":false});
            extrude(context, id + "F17", {"entities" : qUnion([Q0, Q1, Q2, Q3, Q4, Q5, Q6, Q7]), "endBound" : BoundingType.UP_TO_SURFACE, "depth" : 25 * mm, "endBoundEntityFace" : qUnion([Q8]), "offsetDistance" : 25 * mm});
        }
    });
